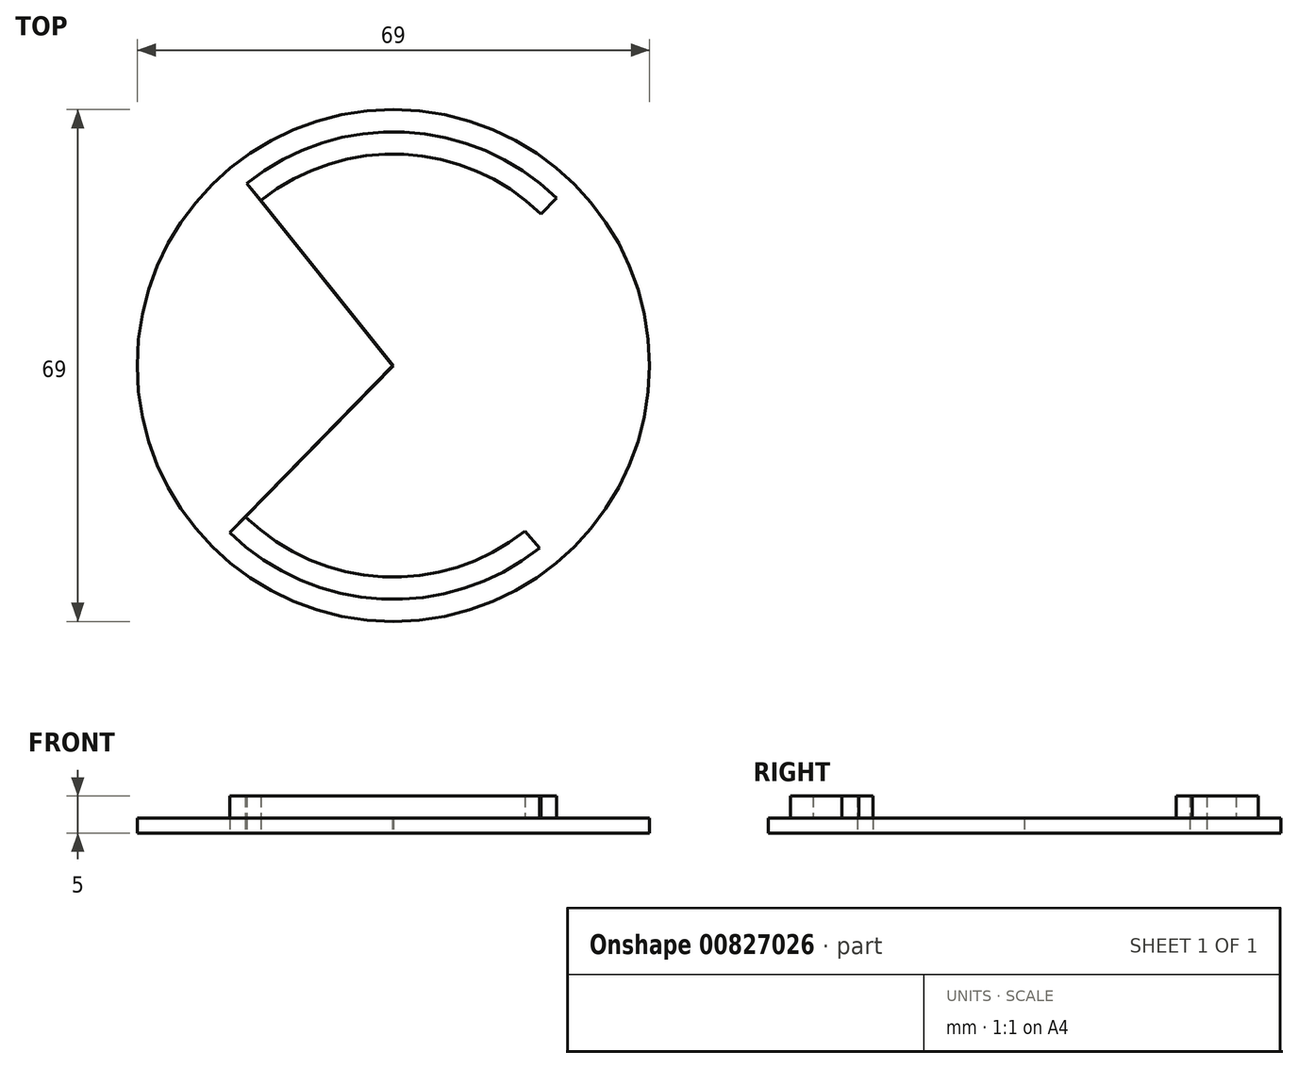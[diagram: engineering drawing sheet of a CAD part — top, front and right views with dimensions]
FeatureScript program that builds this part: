
annotation { "Feature Type Name" : "Feature", "Feature Type Description" : "" }
export const myFeature = defineFeature(function(context is Context, id is Id, definition is map)
    precondition{}
    {
        {
            var Q0;
            Q0=qCreatedBy(makeId("Top.planeOp"),FACE);
            var sketch = newSketch(context, id + "F0", { "sketchPlane" : qUnion([Q0])});
            skLineSegment(sketch, "E0", {"start": v(0, 0) * mm, "end": v(34.5, 0) * mm});
            skCircle(sketch, "E1", {"center": v(0, 0) * mm, "radius": 34.5 * mm});
            skLineSegment(sketch, "E2", {"start": v(34.5, 0) * mm, "end": v(31.5, 0) * mm});
            skCircle(sketch, "E3", {"center": v(0, 0) * mm, "radius": 31.5 * mm});
            skLineSegment(sketch, "E4", {"start": v(31.5, 0) * mm, "end": v(28.5, 0) * mm});
            skCircle(sketch, "E5", {"center": v(0, 0) * mm, "radius": 28.5 * mm});
            skLineSegment(sketch, "E6", {"start": v(0, 0) * mm, "end": v(-17.81, 22.25) * mm});
            skLineSegment(sketch, "E7", {"start": v(-17.81, 22.25) * mm, "end": v(-19.76, 24.53) * mm});
            skLineSegment(sketch, "E8", {"start": v(-19.76, 24.53) * mm, "end": v(17.74, -22.3) * mm});
            skLineSegment(sketch, "E9", {"start": v(17.74, -22.3) * mm, "end": v(19.69, -24.6) * mm});
            skLineSegment(sketch, "E10", {"start": v(0, 0) * mm, "end": v(-19.91, -20.39) * mm});
            skLineSegment(sketch, "E11", {"start": v(-19.91, -20.39) * mm, "end": v(-22.05, -22.5) * mm});
            skLineSegment(sketch, "E12", {"start": v(-22.05, -22.5) * mm, "end": v(19.87, 20.43) * mm});
            skLineSegment(sketch, "E13", {"start": v(19.87, 20.43) * mm, "end": v(21.97, 22.57) * mm});
            skLineSegment(sketch, "E14", {"start": v(-17.81, 22.25) * mm, "end": v(-17.88, 22.2) * mm});
            skSolve(sketch);
        }
        {
            var Q0;
            Q0=makeQuery(id+"F0.imprint","IMPRINT",FACE,{"disambiguationData":[TD([[makeQuery(id+"F0.imprint","IMPRINT",EDGE,{"derivedFrom":sQuery(id+"F0.wireOp",EDGE,"E1")}),1.0]])]});
            var Q1;
            {var subQ0=sQuery(id+"F0.wireOp",EDGE,"E8");var subQ5=sQuery(id+"F0.wireOp",EDGE,"E5");var subQ6=makeQuery(id+"F0.imprint","INTERSECT",VERTEX,{"derivedFrom":[subQ5,subQ0]});Q1=makeQuery(id+"F0.imprint","IMPRINT",FACE,{"disambiguationData":[TD([[makeQuery(id+"F0.imprint","IMPRINT",EDGE,{"disambiguationData":[TD([[subQ6,-1.0]])],"derivedFrom":subQ5}),-1.0]])]});}
            var Q2;
            {var subQ0=sQuery(id+"F0.wireOp",EDGE,"E8");var subQ1=sQuery(id+"F0.wireOp",EDGE,"E5");var subQ2=makeQuery(id+"F0.imprint","INTERSECT",VERTEX,{"derivedFrom":[subQ1,subQ0]});Q2=makeQuery(id+"F0.imprint","IMPRINT",FACE,{"disambiguationData":[TD([[makeQuery(id+"F0.imprint","IMPRINT",EDGE,{"disambiguationData":[TD([[subQ2,-1.0]])],"derivedFrom":subQ1}),1.0]])]});}
            var Q3;
            {var subQ0=sQuery(id+"F0.wireOp",EDGE,"E6");var subQ3=sQuery(id+"F0.wireOp",EDGE,"E12");var subQ5=makeQuery(id+"F0.imprint","INTERSECT",VERTEX,{"derivedFrom":[subQ0,subQ3]});Q3=makeQuery(id+"F0.imprint","IMPRINT",FACE,{"disambiguationData":[TD([[makeQuery(id+"F0.imprint","IMPRINT",EDGE,{"disambiguationData":[TD([[subQ5,-1.0]])],"derivedFrom":subQ0}),-1.0]])]});}
            var Q4;
            {var subQ0=sQuery(id+"F0.wireOp",EDGE,"E0");Q4=makeQuery(id+"F0.imprint","IMPRINT",FACE,{"disambiguationData":[TD([[makeQuery(id+"F0.imprint","IMPRINT",EDGE,{"derivedFrom":subQ0}),1.0]])]});}
            var Q5;
            {var subQ0=sQuery(id+"F0.wireOp",EDGE,"E0");Q5=makeQuery(id+"F0.imprint","IMPRINT",FACE,{"disambiguationData":[TD([[makeQuery(id+"F0.imprint","IMPRINT",EDGE,{"derivedFrom":subQ0}),-1.0]])]});}
            var Q6;
            {var subQ0=sQuery(id+"F0.wireOp",EDGE,"E8");var subQ3=sQuery(id+"F0.wireOp",EDGE,"E10");var subQ5=makeQuery(id+"F0.imprint","INTERSECT",VERTEX,{"derivedFrom":[subQ0,subQ3]});Q6=makeQuery(id+"F0.imprint","IMPRINT",FACE,{"disambiguationData":[TD([[makeQuery(id+"F0.imprint","IMPRINT",EDGE,{"disambiguationData":[TD([[subQ5,-1.0]])],"derivedFrom":subQ0}),-1.0]])]});}
            var Q7;
            {var subQ0=sQuery(id+"F0.wireOp",EDGE,"E4");Q7=makeQuery(id+"F0.imprint","IMPRINT",FACE,{"disambiguationData":[TD([[makeQuery(id+"F0.imprint","IMPRINT",EDGE,{"derivedFrom":subQ0}),1.0]])]});}
            var Q8;
            {var subQ0=sQuery(id+"F0.wireOp",EDGE,"E4");Q8=makeQuery(id+"F0.imprint","IMPRINT",FACE,{"disambiguationData":[TD([[makeQuery(id+"F0.imprint","IMPRINT",EDGE,{"derivedFrom":subQ0}),-1.0]])]});}
            extrude(context, id + "F1", {"entities" : qUnion([Q0, Q1, Q2, Q3, Q4, Q5, Q6, Q7, Q8]), "depth" : 2 * mm, "offsetDistance" : 25 * mm});
        }
        {
            var Q0;
            {var subQ0=sQuery(id+"F0.wireOp",EDGE,"E7");Q0=makeQuery(id+"F0.imprint","IMPRINT",FACE,{"disambiguationData":[TD([[makeQuery(id+"F0.imprint","IMPRINT",EDGE,{"derivedFrom":subQ0}),-1.0]])]});}
            var Q1;
            {var subQ0=sQuery(id+"F0.wireOp",EDGE,"E9");Q1=makeQuery(id+"F0.imprint","IMPRINT",FACE,{"disambiguationData":[TD([[makeQuery(id+"F0.imprint","IMPRINT",EDGE,{"derivedFrom":subQ0}),-1.0]])]});}
            extrude(context, id + "F2", {"entities" : qUnion([Q0, Q1]), "operationType" : NewBodyOperationType.ADD, "depth" : 5 * mm, "offsetDistance" : 25 * mm});
        }
    });
